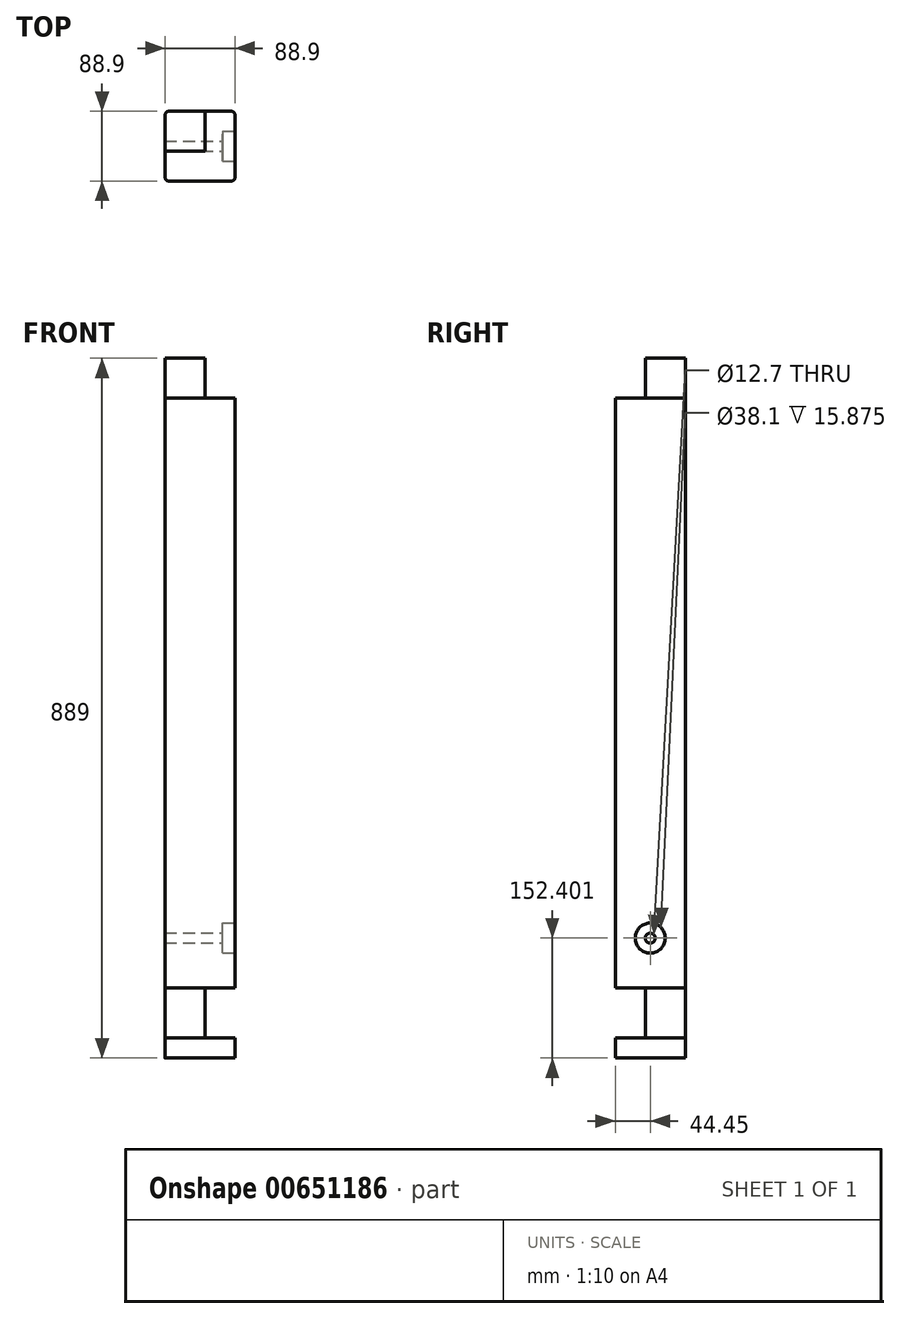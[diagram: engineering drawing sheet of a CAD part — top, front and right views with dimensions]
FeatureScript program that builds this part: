
annotation { "Feature Type Name" : "Feature", "Feature Type Description" : "" }
export const myFeature = defineFeature(function(context is Context, id is Id, definition is map)
    precondition{}
    {
        {
            var Q0;
            Q0=qCreatedBy(makeId("Right.planeOp"),FACE);
            var sketch = newSketch(context, id + "F0", { "sketchPlane" : qUnion([Q0])});
            skLineSegment(sketch, "E0", {"start": v(26.36, 525) * mm, "end": v(26.36, -364) * mm});
            skLineSegment(sketch, "E1", {"start": v(26.36, -364) * mm, "end": v(-62.54, -364) * mm});
            skLineSegment(sketch, "E2", {"start": v(-62.54, -364) * mm, "end": v(-62.54, -338.6) * mm});
            skLineSegment(sketch, "E3", {"start": v(-62.54, -338.6) * mm, "end": v(-24.44, -338.6) * mm});
            skLineSegment(sketch, "E4", {"start": v(-24.44, -338.6) * mm, "end": v(-24.44, -275.1) * mm});
            skLineSegment(sketch, "E5", {"start": v(-24.44, -275.1) * mm, "end": v(-62.54, -275.1) * mm});
            skLineSegment(sketch, "E6", {"start": v(-62.54, -275.1) * mm, "end": v(-62.54, 474.2) * mm});
            skLineSegment(sketch, "E7", {"start": v(-62.54, 474.2) * mm, "end": v(-24.44, 474.2) * mm});
            skLineSegment(sketch, "E8", {"start": v(-24.44, 474.2) * mm, "end": v(-24.44, 525) * mm});
            skLineSegment(sketch, "E9", {"start": v(-24.44, 525) * mm, "end": v(26.36, 525) * mm});
            skSolve(sketch);
        }
        {
            var Q0;
            Q0=makeQuery(id+"F0.imprint","IMPRINT",FACE,{"disambiguationData":[TD([[makeQuery(id+"F0.imprint","IMPRINT",EDGE,{"derivedFrom":sQuery(id+"F0.wireOp",EDGE,"E0")}),-1.0]])]});
            extrude(context, id + "F1", {"entities" : qUnion([Q0]), "depth" : 88.9 * mm, "offsetDistance" : 25.4 * mm, "symmetric" : true});
        }
        {
            var Q0;
            Q0=makeQuery(id+"F1.opExtrude","CAP_EDGE",EDGE,{"disambiguationData":[OSD([sQuery(id+"F0.wireOp",EDGE,"E6")])],"isStart":false});
            var Q1;
            Q1=makeQuery(id+"F1.opExtrude","CAP_EDGE",EDGE,{"disambiguationData":[OSD([sQuery(id+"F0.wireOp",EDGE,"E2")])],"isStart":false});
            var Q2;
            Q2=makeQuery(id+"F1.opExtrude","CAP_EDGE",EDGE,{"disambiguationData":[OSD([sQuery(id+"F0.wireOp",EDGE,"E2")])],"isStart":true});
            var Q3;
            Q3=makeQuery(id+"F1.opExtrude","CAP_EDGE",EDGE,{"disambiguationData":[OSD([sQuery(id+"F0.wireOp",EDGE,"E6")])],"isStart":true});
            var Q4;
            Q4=makeQuery(id+"F1.opExtrude","CAP_EDGE",EDGE,{"disambiguationData":[OSD([sQuery(id+"F0.wireOp",EDGE,"E0")])],"isStart":false});
            var Q5;
            Q5=makeQuery(id+"F1.opExtrude","CAP_EDGE",EDGE,{"disambiguationData":[OSD([sQuery(id+"F0.wireOp",EDGE,"E0")])],"isStart":true});
            fillet(context, id + "F2", {"entities" : qUnion([Q0, Q1, Q2, Q3, Q4, Q5]), "radius" : 5.08 * mm, "tangentPropagation" : true, "allowEdgeOverflow" : false});
        }
        {
            var Q0;
            Q0=qCreatedBy(makeId("Front.planeOp"),FACE);
            var sketch = newSketch(context, id + "F3", { "sketchPlane" : qUnion([Q0])});
            skLineSegment(sketch, "E10.0", {"start": v(44.45, 525) * mm, "end": v(6.35, 525) * mm});
            skLineSegment(sketch, "E11.0", {"start": v(44.45, 474.2) * mm, "end": v(44.45, 525) * mm});
            skLineSegment(sketch, "E12.0", {"start": v(39.37, 474.2) * mm, "end": v(6.35, 474.2) * mm});
            skLineSegment(sketch, "E13.0", {"start": v(39.37, 474.2) * mm, "end": v(44.45, 474.2) * mm});
            skLineSegment(sketch, "E14", {"start": v(6.35, 525) * mm, "end": v(6.35, 474.2) * mm});
            skLineSegment(sketch, "E15.0", {"start": v(39.37, -275.1) * mm, "end": v(6.35, -275.1) * mm});
            skLineSegment(sketch, "E16.0", {"start": v(44.45, -275.1) * mm, "end": v(39.37, -275.1) * mm});
            skLineSegment(sketch, "E17.0", {"start": v(44.45, -338.6) * mm, "end": v(44.45, -275.1) * mm});
            skLineSegment(sketch, "E18.0", {"start": v(39.37, -338.6) * mm, "end": v(6.35, -338.6) * mm});
            skLineSegment(sketch, "E19.0", {"start": v(39.37, -338.6) * mm, "end": v(44.45, -338.6) * mm});
            skLineSegment(sketch, "E20", {"start": v(6.35, -275.1) * mm, "end": v(6.35, -338.6) * mm});
            skSolve(sketch);
        }
        {
            var Q0;
            Q0 = qSketchRegion(id + "F3", true);
            extrude(context, id + "F4", {"entities" : qUnion([Q0]), "operationType" : NewBodyOperationType.REMOVE, "oppositeDirection" : true, "depth" : 101.6 * mm, "offsetDistance" : 25.4 * mm, "symmetric" : true});
        }
        {
            var Q0;
            Q0=qCreatedBy(makeId("Right.planeOp"),FACE);
            var sketch = newSketch(context, id + "F5", { "sketchPlane" : qUnion([Q0])});
            skCircle(sketch, "E21", {"center": v(-18.1, -211.6) * mm, "radius": 6.35 * mm});
            skSolve(sketch);
        }
        {
            var Q0;
            Q0 = qSketchRegion(id + "F5", true);
            extrude(context, id + "F6", {"entities" : qUnion([Q0]), "operationType" : NewBodyOperationType.REMOVE, "endBound" : BoundingType.THROUGH_ALL, "oppositeDirection" : true, "depth" : 25.4 * mm, "offsetDistance" : 25.4 * mm, "hasSecondDirection" : true, "secondDirectionBound" : BoundingType.THROUGH_ALL, "secondDirectionOppositeDirection" : false, "secondDirectionDepth" : 25.4 * mm});
        }
        {
            var Q0;
            {var subQ0=sQuery(id+"F0.wireOp",EDGE,"E6");var subQ1=sQuery(id+"F0.wireOp",EDGE,"E7");var subQ2=sQuery(id+"F0.wireOp",EDGE,"E0");var subQ3=sQuery(id+"F0.wireOp",EDGE,"E5");Q0=makeQuery(id+"F4.boolean.opBoolean","SPLIT",FACE,{"disambiguationData":[TD([makeQuery(id+"F1.opExtrude","SWEPT_FACE",FACE,{"disambiguationData":[OSD([subQ3])]})])],"derivedFrom":makeQuery(id+"F1.opExtrude","CAP_FACE",FACE,{"disambiguationData":[OSD([subQ2,sQuery(id+"F0.wireOp",EDGE,"E1"),sQuery(id+"F0.wireOp",EDGE,"E2"),sQuery(id+"F0.wireOp",EDGE,"E3"),sQuery(id+"F0.wireOp",EDGE,"E4"),subQ3,subQ0,subQ1,sQuery(id+"F0.wireOp",EDGE,"E8"),sQuery(id+"F0.wireOp",EDGE,"E9")])],"isStart":false})});}
            var sketch = newSketch(context, id + "F7", { "sketchPlane" : qUnion([Q0])});
            skCircle(sketch, "E22", {"center": v(-18.1, -211.6) * mm, "radius": 19.05 * mm});
            skSolve(sketch);
        }
        {
            var Q0;
            Q0=makeQuery(id+"F7.imprint","IMPRINT",FACE,{"disambiguationData":[TD([[makeQuery(id+"F7.imprint","IMPRINT",EDGE,{"derivedFrom":sQuery(id+"F7.wireOp",EDGE,"E22")}),1.0]])]});
            extrude(context, id + "F8", {"entities" : qUnion([Q0]), "operationType" : NewBodyOperationType.REMOVE, "oppositeDirection" : true, "depth" : 15.88 * mm, "offsetDistance" : 25.4 * mm});
        }
    });
